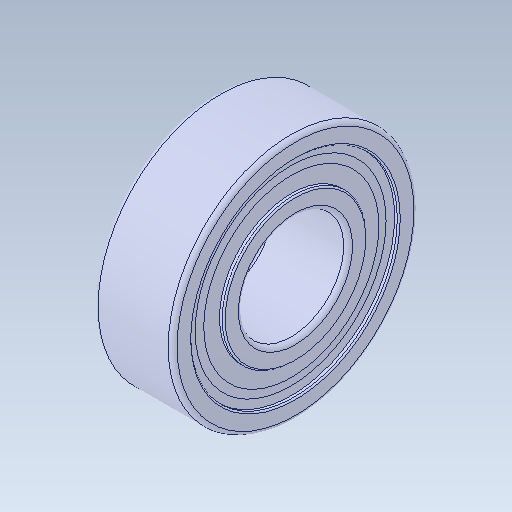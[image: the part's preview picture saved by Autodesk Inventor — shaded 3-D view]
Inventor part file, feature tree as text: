
AUTODESK INVENTOR PART (.ipt)
format: ipt  version: 2020 (Build 240168000, 168)  size: 222,208 bytes
history: native  units: in
note: dims shown in document units (in); Inventor stores cm internally (conversion verified against a paired STEP export)
features: revolve x1
ambient origin geometry x8: Origin, YZ Plane, XZ Plane, XY Plane, X Axis, Y Axis, Z Axis, Center Point
bodies: Solid1 (feature_tree)
feature tree (1):
  revolve  "Revolve1"  [1 undecoded]
note: 1 required parameter value undecoded (feature->parameter linkage not recoverable at this tier; creation-order binding heuristic only, values carry confidence <= 0.55)
